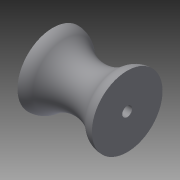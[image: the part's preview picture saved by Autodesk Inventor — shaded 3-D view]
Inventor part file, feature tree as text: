
AUTODESK INVENTOR PART (.ipt)
format: ipt  version: 2015 (Build 190159000, 159)  size: 207,360 bytes
history: native  units: mm
features: sketch x2, revolve x1, extrude x1, fillet x1
ambient origin geometry x8: Origin, YZ Plane, XZ Plane, XY Plane, X Axis, Y Axis, Z Axis, Center Point
bodies: Solid1 (feature_tree)
feature tree (5):
  revolve  "Revolution1"  [1 undecoded]
  extrude  "Extrusion1"  Depth=7.0mm
  fillet  "Fillet2"  Radius=52.7mm
  sketch  "Sketch1"  dims[d2=5.0mm d4=5.0mm]
  sketch  "Sketch2"  dims[d7=90.0deg d8=7.0mm d9=52.7mm d10=0.0mm d12=12.0mm]
note: 1 required parameter value undecoded (feature->parameter linkage not recoverable at this tier; creation-order binding heuristic only, values carry confidence <= 0.55)
